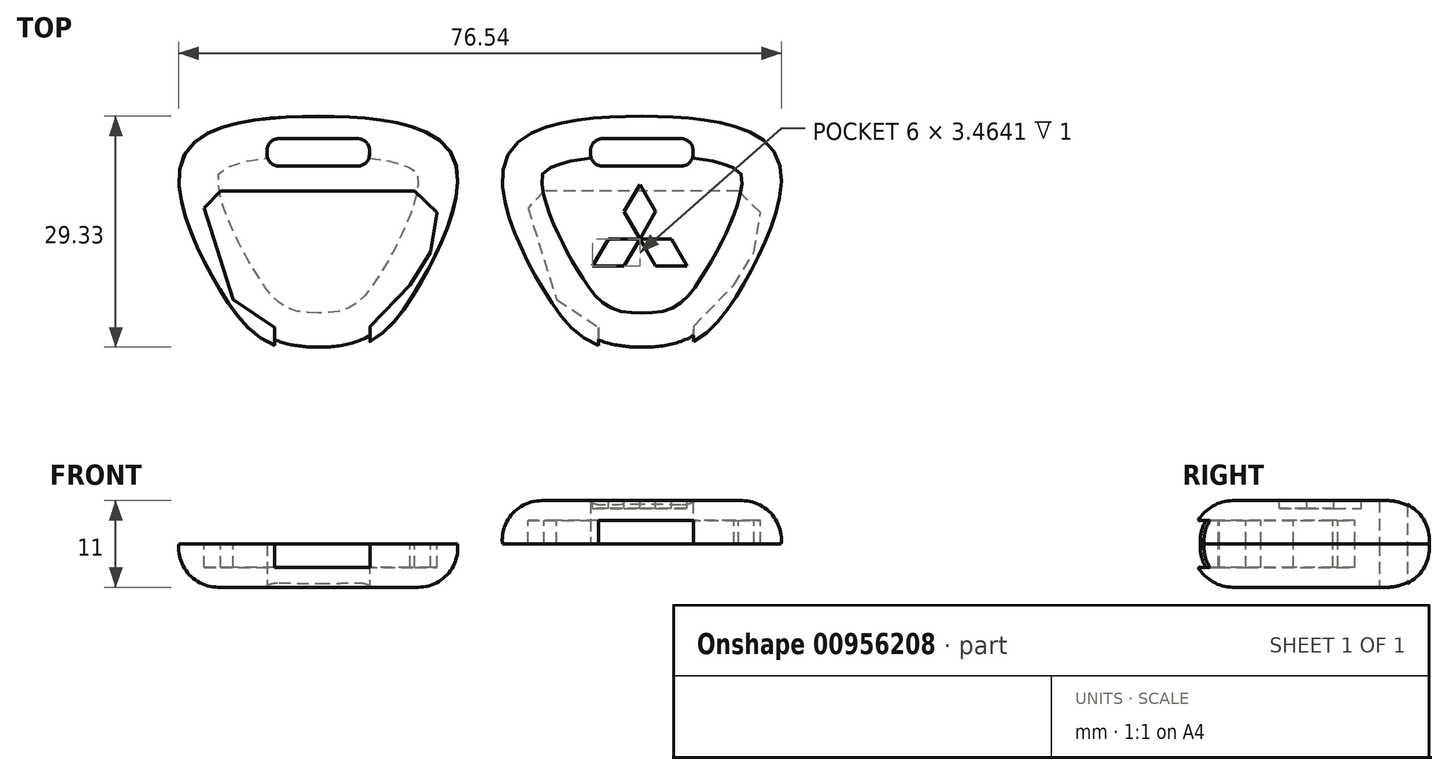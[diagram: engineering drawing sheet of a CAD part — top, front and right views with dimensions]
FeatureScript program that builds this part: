
annotation { "Feature Type Name" : "Feature", "Feature Type Description" : "" }
export const myFeature = defineFeature(function(context is Context, id is Id, definition is map)
    precondition{}
    {
        {
            var Q0;
            Q0=qCreatedBy(makeId("Top.planeOp"),FACE);
            var sketch = newSketch(context, id + "F0", { "sketchPlane" : qUnion([Q0])});
            skFitSpline(sketch, "E0", {"points": [v(0, 30) * mm, v(17.5, 23.85) * mm, v(12.05, 7.26) * mm, v(0, 0) * mm], "startDerivative": vector(87.42, 0) * mm, "endDerivative": vector(-65.74, 0) * mm});
            skFitSpline(sketch, "E1.MirrorCS", {"points": [v(0, 30) * mm, v(-17.5, 23.85) * mm, v(-12.05, 7.26) * mm, v(0, 0) * mm], "startDerivative": vector(-87.42, 0) * mm, "endDerivative": vector(65.74, 0) * mm});
            skLineSegment(sketch, "E2", {"start": v(0, 27.16) * mm, "end": v(5, 27.16) * mm});
            skLineSegment(sketch, "E3", {"start": v(6.5, 25.66) * mm, "end": v(6.5, 25.16) * mm});
            skLineSegment(sketch, "E4", {"start": v(5, 23.66) * mm, "end": v(0, 23.66) * mm});
            skPoint(sketch, "E5.visualSharp", {"position": v(6.5, 27.16) * mm});
            skArc(sketch, "E5.filletArc", {"start": v(6.5, 25.66) * mm, "mid": v(6.06, 26.73) * mm, "end": v(5, 27.16) * mm});
            skPoint(sketch, "E6.visualSharp", {"position": v(6.5, 23.66) * mm});
            skArc(sketch, "E6.filletArc", {"start": v(5, 23.66) * mm, "mid": v(6.06, 24.1) * mm, "end": v(6.5, 25.16) * mm});
            skLineSegment(sketch, "E7.MirrorCS", {"start": v(-6.5, 25.66) * mm, "end": v(-6.5, 25.16) * mm});
            skArc(sketch, "E8.MirrorCS", {"start": v(-5, 23.66) * mm, "mid": v(-6.06, 24.1) * mm, "end": v(-6.5, 25.16) * mm});
            skArc(sketch, "E9.MirrorCS", {"start": v(-6.5, 25.66) * mm, "mid": v(-6.06, 26.73) * mm, "end": v(-5, 27.16) * mm});
            skPoint(sketch, "E10.MirrorP", {"position": v(-6.5, 23.66) * mm});
            skLineSegment(sketch, "E11.MirrorCS", {"start": v(-5, 23.66) * mm, "end": v(0, 23.66) * mm});
            skLineSegment(sketch, "E12.MirrorCS", {"start": v(0, 27.16) * mm, "end": v(-5, 27.16) * mm});
            skPoint(sketch, "E13.MirrorP", {"position": v(-6.5, 27.16) * mm});
            skSolve(sketch);
        }
        {
            var Q0;
            Q0 = qSketchRegion(id + "F0", true);
            extrude(context, id + "F1", {"entities" : qUnion([Q0]), "depth" : 10 * mm, "offsetDistance" : 25 * mm});
        }
        {
            var Q0;
            Q0=makeQuery(id+"F1.opExtrude","CAP_EDGE",EDGE,{"disambiguationData":[OSD([sQuery(id+"F0.wireOp",EDGE,"E0")])],"isStart":false});
            var Q1;
            Q1=makeQuery(id+"F1.opExtrude","CAP_EDGE",EDGE,{"disambiguationData":[OSD([sQuery(id+"F0.wireOp",EDGE,"E0")])],"isStart":true});
            fillet(context, id + "F2", {"entities" : qUnion([Q0, Q1]), "radius" : 5 * mm, "tangentPropagation" : true, "allowEdgeOverflow" : false});
        }
        {
            var Q0;
            Q0=qCreatedBy(makeId("Top.planeOp"),FACE);
            cPlane(context, id + "F3", {"entities" : qUnion([Q0]), "cplaneType" : CPlaneType.OFFSET, "offset" : 5.5 * mm, "width" : 150 * mm, "height" : 150 * mm});
        }
        {
            var Q0;
            Q0=qCreatedBy(id+"F3.planeOp",FACE);
            cPlane(context, id + "F4", {"entities" : qUnion([Q0]), "cplaneType" : CPlaneType.OFFSET, "offset" : 0.5 * mm, "oppositeDirection" : true, "width" : 150 * mm, "height" : 150 * mm});
        }
        {
            var Q0;
            Q0=qCreatedBy(id+"F4.planeOp",FACE);
            var sketch = newSketch(context, id + "F5", { "sketchPlane" : qUnion([Q0])});
            skLineSegment(sketch, "E14", {"start": v(-5.52, -0.1) * mm, "end": v(-5.52, 3.2) * mm});
            skLineSegment(sketch, "E15", {"start": v(-5.52, 3.2) * mm, "end": v(-10.81, 6.7) * mm});
            skLineSegment(sketch, "E16", {"start": v(-10.81, 6.7) * mm, "end": v(-14.48, 18.35) * mm});
            skLineSegment(sketch, "E17", {"start": v(-14.48, 18.35) * mm, "end": v(-12.43, 20.5) * mm});
            skLineSegment(sketch, "E18", {"start": v(-12.43, 20.5) * mm, "end": v(12.26, 20.5) * mm});
            skLineSegment(sketch, "E19", {"start": v(12.26, 20.5) * mm, "end": v(15.08, 17.76) * mm});
            skLineSegment(sketch, "E20", {"start": v(15.08, 17.76) * mm, "end": v(14.27, 12.74) * mm});
            skLineSegment(sketch, "E21", {"start": v(14.27, 12.74) * mm, "end": v(11.68, 8.59) * mm});
            skLineSegment(sketch, "E22", {"start": v(11.68, 8.59) * mm, "end": v(6.56, 3.3) * mm});
            skLineSegment(sketch, "E23", {"start": v(6.56, 3.3) * mm, "end": v(6.56, 0) * mm});
            skLineSegment(sketch, "E24", {"start": v(6.56, 0) * mm, "end": v(-5.52, -0.1) * mm});
            skSolve(sketch);
        }
        {
            var Q0;
            Q0 = qSketchRegion(id + "F5", true);
            extrude(context, id + "F6", {"entities" : qUnion([Q0]), "operationType" : NewBodyOperationType.REMOVE, "oppositeDirection" : true, "depth" : 5 * mm, "offsetDistance" : 25 * mm, "symmetric" : true});
        }
        {
            var Q0;
            Q0=makeQuery(id+"F1.opExtrude","SWEPT_BODY",BODY,{"disambiguationData":[OSD([sQuery(id+"F0.wireOp",EDGE,"E0"),sQuery(id+"F0.wireOp",EDGE,"E1.MirrorCS"),sQuery(id+"F0.wireOp",EDGE,"E2"),sQuery(id+"F0.wireOp",EDGE,"E3"),sQuery(id+"F0.wireOp",EDGE,"E4"),sQuery(id+"F0.wireOp",EDGE,"E5.filletArc"),sQuery(id+"F0.wireOp",EDGE,"E6.filletArc"),sQuery(id+"F0.wireOp",EDGE,"E7.MirrorCS"),sQuery(id+"F0.wireOp",EDGE,"E8.MirrorCS"),sQuery(id+"F0.wireOp",EDGE,"E9.MirrorCS"),sQuery(id+"F0.wireOp",EDGE,"E11.MirrorCS"),sQuery(id+"F0.wireOp",EDGE,"E12.MirrorCS")])]});
            transform(context, id + "F7", {"entities" : qUnion([Q0]), "transformType" : TransformType.TRANSLATION_3D, "dx" : 41.1 * mm, "dy" : 0 * mm, "dz" : 1 * mm, "makeCopy" : true});
        }
        {
            var Q0;
            Q0=qCreatedBy(id+"F3.planeOp",FACE);
            var sketch = newSketch(context, id + "F8", { "sketchPlane" : qUnion([Q0])});
            skLineSegment(sketch, "E25.bottom", {"start": v(-26.04, 32.93) * mm, "end": v(20.32, 32.93) * mm});
            skLineSegment(sketch, "E25.top", {"start": v(-26.04, 0) * mm, "end": v(20.32, 0) * mm});
            skLineSegment(sketch, "E25.left", {"start": v(-26.04, 32.93) * mm, "end": v(-26.04, 0) * mm});
            skLineSegment(sketch, "E25.right", {"start": v(20.32, 32.93) * mm, "end": v(20.32, 0) * mm});
            skSolve(sketch);
        }
        {
            var Q0;
            Q0 = qSketchRegion(id + "F8", true);
            extrude(context, id + "F9", {"entities" : qUnion([Q0]), "operationType" : NewBodyOperationType.REMOVE, "flatOperationType" : FlatOperationType.REMOVE, "depth" : 5 * mm, "offsetDistance" : 25 * mm, "domain" : OperationDomain.MODEL});
        }
        {
            var Q0;
            Q0=makeQuery(id+"F7.opPattern","COPY",FACE,{"derivedFrom":makeQuery(id+"F1.opExtrude","CAP_FACE",FACE,{"disambiguationData":[OSD([sQuery(id+"F0.wireOp",EDGE,"E0"),sQuery(id+"F0.wireOp",EDGE,"E1.MirrorCS"),sQuery(id+"F0.wireOp",EDGE,"E2"),sQuery(id+"F0.wireOp",EDGE,"E3"),sQuery(id+"F0.wireOp",EDGE,"E4"),sQuery(id+"F0.wireOp",EDGE,"E5.filletArc"),sQuery(id+"F0.wireOp",EDGE,"E6.filletArc"),sQuery(id+"F0.wireOp",EDGE,"E7.MirrorCS"),sQuery(id+"F0.wireOp",EDGE,"E8.MirrorCS"),sQuery(id+"F0.wireOp",EDGE,"E9.MirrorCS"),sQuery(id+"F0.wireOp",EDGE,"E11.MirrorCS"),sQuery(id+"F0.wireOp",EDGE,"E12.MirrorCS")])],"isStart":false}),"instanceName":"1"});
            var sketch = newSketch(context, id + "F10", { "sketchPlane" : qUnion([Q0])});
            skLineSegment(sketch, "E26", {"start": v(34.85, 10.95) * mm, "end": v(38.85, 10.95) * mm});
            skLineSegment(sketch, "E27", {"start": v(38.85, 10.95) * mm, "end": v(40.85, 14.41) * mm});
            skLineSegment(sketch, "E28", {"start": v(40.85, 14.41) * mm, "end": v(36.85, 14.41) * mm});
            skLineSegment(sketch, "E29", {"start": v(36.85, 14.41) * mm, "end": v(34.85, 10.95) * mm});
            skLineSegment(sketch, "E30", {"start": v(40.86, 14.42) * mm, "end": v(42.86, 17.88) * mm});
            skLineSegment(sketch, "E31", {"start": v(42.86, 17.88) * mm, "end": v(40.86, 21.35) * mm});
            skLineSegment(sketch, "E32", {"start": v(40.86, 21.35) * mm, "end": v(38.86, 17.88) * mm});
            skLineSegment(sketch, "E33", {"start": v(38.86, 17.88) * mm, "end": v(40.86, 14.42) * mm});
            skLineSegment(sketch, "E34", {"start": v(40.86, 14.43) * mm, "end": v(42.86, 10.96) * mm});
            skLineSegment(sketch, "E35", {"start": v(42.86, 10.96) * mm, "end": v(46.86, 10.96) * mm});
            skLineSegment(sketch, "E36", {"start": v(46.86, 10.96) * mm, "end": v(44.86, 14.43) * mm});
            skLineSegment(sketch, "E37", {"start": v(44.86, 14.43) * mm, "end": v(40.86, 14.43) * mm});
            skSolve(sketch);
        }
        {
            var Q0;
            Q0 = qSketchRegion(id + "F10", true);
            extrude(context, id + "F11", {"entities" : qUnion([Q0]), "operationType" : NewBodyOperationType.REMOVE, "oppositeDirection" : true, "depth" : 1 * mm, "offsetDistance" : 25 * mm});
        }
        {
            var Q0;
            Q0=qCreatedBy(id+"F3.planeOp",FACE);
            var sketch = newSketch(context, id + "F12", { "sketchPlane" : qUnion([Q0])});
            skLineSegment(sketch, "E38.bottom", {"start": v(63.42, 31.66) * mm, "end": v(20.05, 31.66) * mm});
            skLineSegment(sketch, "E38.top", {"start": v(63.42, -1.36) * mm, "end": v(20.05, -1.36) * mm});
            skLineSegment(sketch, "E38.left", {"start": v(63.42, 31.66) * mm, "end": v(63.42, -1.36) * mm});
            skLineSegment(sketch, "E38.right", {"start": v(20.05, 31.66) * mm, "end": v(20.05, -1.36) * mm});
            skSolve(sketch);
        }
        {
            var Q0;
            Q0 = qSketchRegion(id + "F12", true);
            extrude(context, id + "F13", {"entities" : qUnion([Q0]), "operationType" : NewBodyOperationType.REMOVE, "oppositeDirection" : true, "depth" : 5 * mm, "offsetDistance" : 25 * mm});
        }
    });
